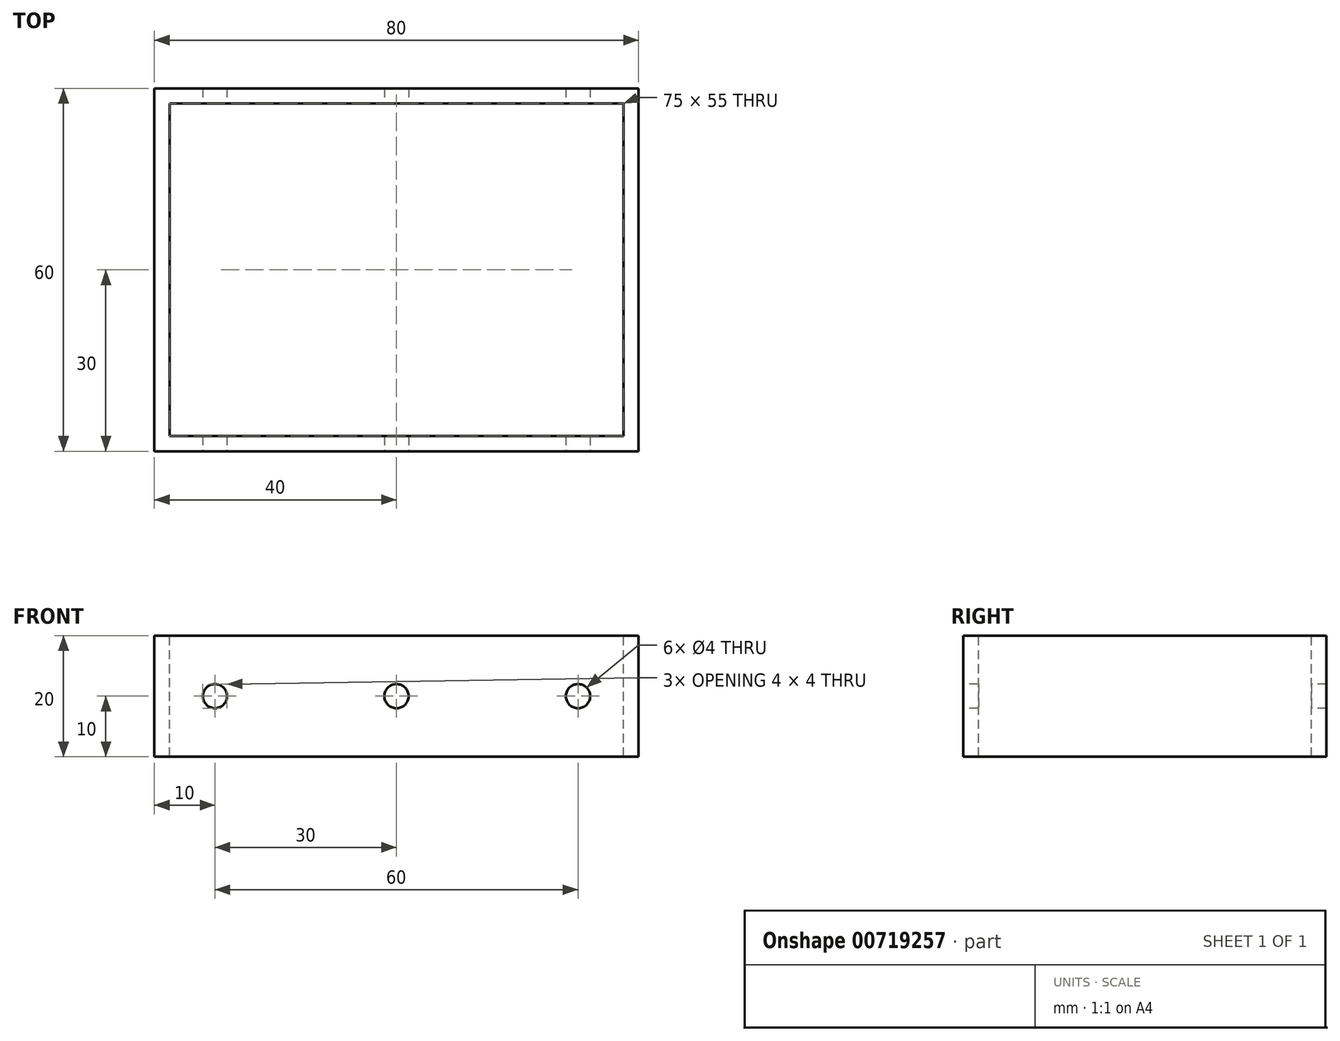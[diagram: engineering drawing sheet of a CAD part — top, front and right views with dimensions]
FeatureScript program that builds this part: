
annotation { "Feature Type Name" : "Feature", "Feature Type Description" : "" }
export const myFeature = defineFeature(function(context is Context, id is Id, definition is map)
    precondition{}
    {
        {
            var Q0;
            Q0=qCreatedBy(makeId("Top.planeOp"),FACE);
            var sketch = newSketch(context, id + "F0", { "sketchPlane" : qUnion([Q0])});
            skLineSegment(sketch, "E0.bottom", {"start": v(40, -30) * mm, "end": v(-40, -30) * mm});
            skLineSegment(sketch, "E0.top", {"start": v(40, 30) * mm, "end": v(-40, 30) * mm});
            skLineSegment(sketch, "E0.left", {"start": v(40, -30) * mm, "end": v(40, 30) * mm});
            skLineSegment(sketch, "E0.right", {"start": v(-40, -30) * mm, "end": v(-40, 30) * mm});
            skPoint(sketch, "E0.middle", {"position": v(0, 0) * mm});
            skSolve(sketch);
        }
        {
            var Q0;
            Q0 = qSketchRegion(id + "F0", true);
            extrude(context, id + "F1", {"entities" : qUnion([Q0]), "depth" : 20 * mm, "offsetDistance" : 25.4 * mm});
        }
        {
            var Q0;
            Q0=makeQuery(id+"F1.opExtrude","CAP_FACE",FACE,{"disambiguationData":[OSD([sQuery(id+"F0.wireOp",EDGE,"E0.bottom"),sQuery(id+"F0.wireOp",EDGE,"E0.top"),sQuery(id+"F0.wireOp",EDGE,"E0.left"),sQuery(id+"F0.wireOp",EDGE,"E0.right")])],"isStart":false});
            var sketch = newSketch(context, id + "F2", { "sketchPlane" : qUnion([Q0])});
            skLineSegment(sketch, "E1.bottom", {"start": v(37.5, 27.5) * mm, "end": v(-37.5, 27.5) * mm});
            skLineSegment(sketch, "E1.top", {"start": v(37.5, -27.5) * mm, "end": v(-37.5, -27.5) * mm});
            skLineSegment(sketch, "E1.left", {"start": v(37.5, 27.5) * mm, "end": v(37.5, -27.5) * mm});
            skLineSegment(sketch, "E1.right", {"start": v(-37.5, 27.5) * mm, "end": v(-37.5, -27.5) * mm});
            skPoint(sketch, "E1.middle", {"position": v(0, 0) * mm});
            skSolve(sketch);
        }
        {
            var Q0;
            Q0 = qSketchRegion(id + "F2", true);
            extrude(context, id + "F3", {"entities" : qUnion([Q0]), "operationType" : NewBodyOperationType.REMOVE, "endBound" : BoundingType.THROUGH_ALL, "oppositeDirection" : true, "depth" : 25.4 * mm, "offsetDistance" : 25.4 * mm});
        }
        {
            var Q0;
            Q0=makeQuery(id+"F1.opExtrude","SWEPT_FACE",FACE,{"disambiguationData":[OSD([sQuery(id+"F0.wireOp",EDGE,"E0.bottom")])]});
            var sketch = newSketch(context, id + "F4", { "sketchPlane" : qUnion([Q0])});
            skCircle(sketch, "E2", {"center": v(-30, 10) * mm, "radius": 2 * mm});
            skPoint(sketch, "E2.centerSnap0", {"position": v(-40, 10) * mm});
            skCircle(sketch, "E3", {"center": v(0, 10) * mm, "radius": 2 * mm});
            skCircle(sketch, "E4", {"center": v(30, 10) * mm, "radius": 2 * mm});
            skPoint(sketch, "E4.centerSnap0", {"position": v(40, 10) * mm});
            skSolve(sketch);
        }
        {
            var Q0;
            Q0 = qSketchRegion(id + "F4", true);
            extrude(context, id + "F5", {"entities" : qUnion([Q0]), "operationType" : NewBodyOperationType.REMOVE, "endBound" : BoundingType.THROUGH_ALL, "oppositeDirection" : true, "depth" : 25.4 * mm, "offsetDistance" : 25.4 * mm});
        }
    });
